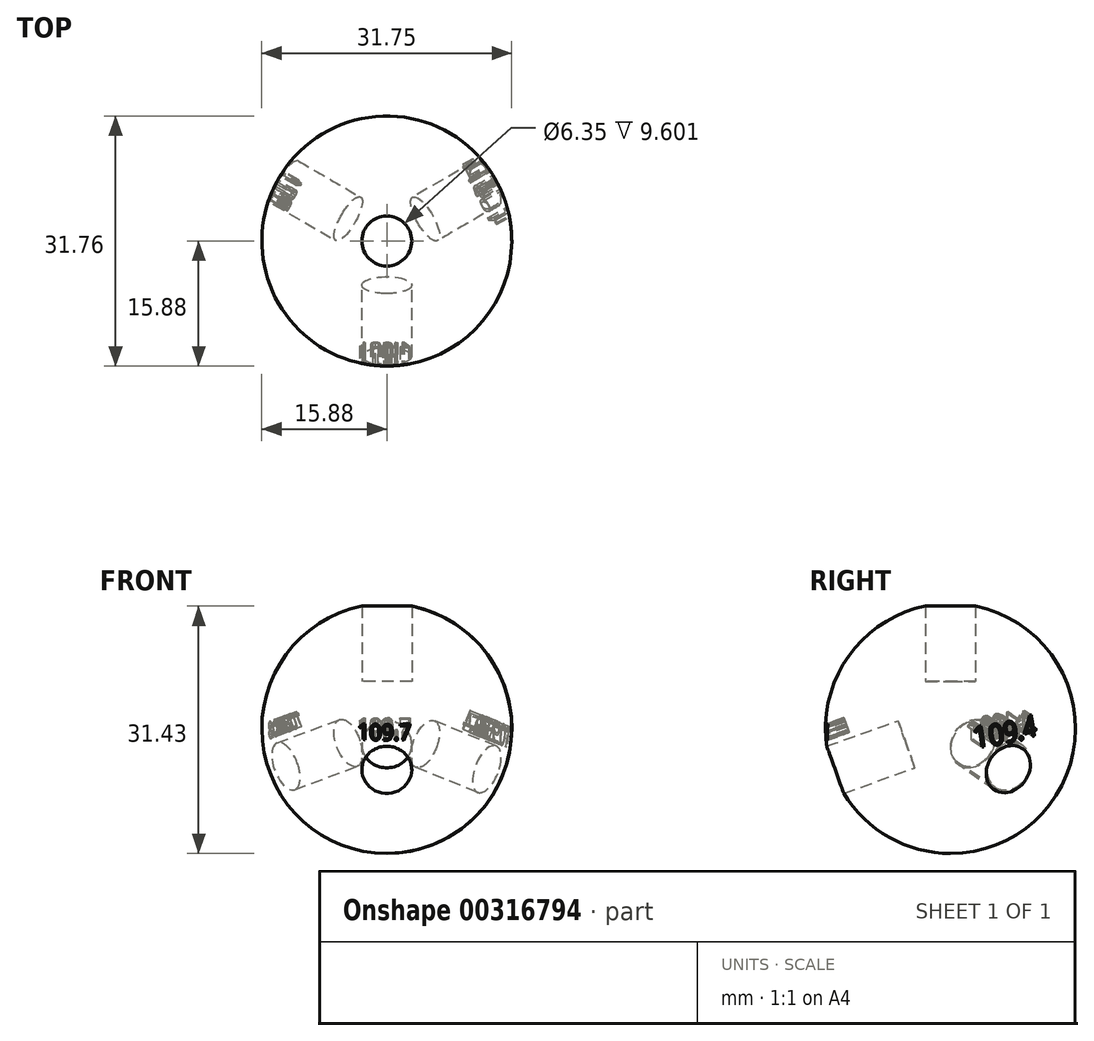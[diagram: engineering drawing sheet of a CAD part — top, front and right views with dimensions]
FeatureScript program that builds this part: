
annotation { "Feature Type Name" : "Feature", "Feature Type Description" : "" }
export const myFeature = defineFeature(function(context is Context, id is Id, definition is map)
    precondition{}
    {
        {
            var Q0;
            Q0=qCreatedBy(makeId("Front.planeOp"),FACE);
            var sketch = newSketch(context, id + "F0", { "sketchPlane" : qUnion([Q0])});
            skArc(sketch, "E0", {"start": v(0, 15.88) * mm, "mid": v(-15.88, 0) * mm, "end": v(0, -15.88) * mm});
            skLineSegment(sketch, "E1", {"start": v(0, 15.88) * mm, "end": v(0, -15.88) * mm});
            skSolve(sketch);
        }
        {
            var Q0;
            Q0 = qSketchRegion(id + "F0", true);
            var Q1;
            Q1=sQuery(id+"F0.wireOp",EDGE,"E1");
            revolve(context, id + "F1", {"entities" : qUnion([Q0]), "axis" : qUnion([Q1]), "revolveType" : RevolveType.FULL});
        }
        {
            var Q0;
            Q0=qCreatedBy(makeId("Top.planeOp"),FACE);
            cPlane(context, id + "F2", {"entities" : qUnion([Q0]), "cplaneType" : CPlaneType.OFFSET, "offset" : 5.95 * mm, "width" : 152.4 * mm, "height" : 152.4 * mm});
        }
        {
            var Q0;
            Q0=qCreatedBy(id+"F2.planeOp",FACE);
            var sketch = newSketch(context, id + "F3", { "sketchPlane" : qUnion([Q0])});
            skCircle(sketch, "E2", {"center": v(0, 0) * mm, "radius": 3.18 * mm});
            skSolve(sketch);
        }
        {
            var Q0;
            Q0 = qSketchRegion(id + "F3", true);
            extrude(context, id + "F4", {"entities" : qUnion([Q0]), "depth" : 25.4 * mm});
        }
        {
            var Q0;
            Q0=qCreatedBy(makeId("Front.planeOp"),FACE);
            var sketch = newSketch(context, id + "F5", { "sketchPlane" : qUnion([Q0])});
            skLineSegment(sketch, "E3", {"start": v(0, 0) * mm, "end": v(0, 41.69) * mm, "construction": true});
            skLineSegment(sketch, "E4", {"start": v(0, 41.69) * mm, "end": v(0, -35) * mm, "construction": true});
            skLineSegment(sketch, "E5", {"start": v(0, 0) * mm, "end": v(-50.95, 0) * mm, "construction": true});
            skLineSegment(sketch, "E6", {"start": v(-50.95, 0) * mm, "end": v(32.52, 0) * mm, "construction": true});
            skSolve(sketch);
        }
        {
            var Q0;
            Q0=qCreatedBy(makeId("Right.planeOp"),FACE);
            var sketch = newSketch(context, id + "F6", { "sketchPlane" : qUnion([Q0])});
            skLineSegment(sketch, "E7", {"start": v(0, 0) * mm, "end": v(52.26, 0) * mm, "construction": true});
            skLineSegment(sketch, "E8", {"start": v(52.26, 0) * mm, "end": v(-49.36, 0) * mm, "construction": true});
            skSolve(sketch);
        }
        {
            var Q0;
            Q0=makeQuery(id+"F4.opExtrude","SWEPT_BODY",BODY,{"disambiguationData":[OSD([sQuery(id+"F3.wireOp",EDGE,"E2")])]});
            var Q1;
            Q1=sQuery(id+"F5.wireOp",EDGE,"E6");
            transform(context, id + "F7", {"entities" : qUnion([Q0]), "transformType" : TransformType.ROTATION, "transformAxis" : qUnion([Q1]), "angle" : 109.7 * degree, "makeCopy" : true});
        }
        {
            var Q0;
            Q0=makeQuery(id+"F4.opExtrude","SWEPT_BODY",BODY,{"disambiguationData":[OSD([sQuery(id+"F3.wireOp",EDGE,"E2")])]});
            var Q1;
            Q1=sQuery(id+"F6.wireOp",EDGE,"E8");
            transform(context, id + "F8", {"entities" : qUnion([Q0]), "transformType" : TransformType.ROTATION, "transformAxis" : qUnion([Q1]), "angle" : 108 * degree, "makeCopy" : true});
        }
        {
            var Q0;
            Q0=makeQuery(id+"F8.opPattern","COPY",BODY,{"derivedFrom":makeQuery(id+"F4.opExtrude","SWEPT_BODY",BODY,{"disambiguationData":[OSD([sQuery(id+"F3.wireOp",EDGE,"E2")])]}),"instanceName":"1"});
            var Q1;
            Q1=sQuery(id+"F5.wireOp",EDGE,"E4");
            transform(context, id + "F9", {"entities" : qUnion([Q0]), "transformType" : TransformType.ROTATION, "transformAxis" : qUnion([Q1]), "angle" : 30 * degree, "makeCopy" : false});
        }
        {
            var Q0;
            Q0=makeQuery(id+"F7.opPattern","COPY",FACE,{"derivedFrom":makeQuery(id+"F4.opExtrude","CAP_FACE",FACE,{"disambiguationData":[OSD([sQuery(id+"F3.wireOp",EDGE,"E2")])],"isStart":false}),"instanceName":"1"});
            cPlane(context, id + "F10", {"entities" : qUnion([Q0]), "cplaneType" : CPlaneType.OFFSET, "offset" : 12.7 * mm, "oppositeDirection" : true, "width" : 152.4 * mm, "height" : 152.4 * mm});
        }
        {
            var Q0;
            Q0=qCreatedBy(id+"F10.planeOp",FACE);
            var sketch = newSketch(context, id + "F11", { "sketchPlane" : qUnion([Q0])});
            skText(sketch, "E9", { "text": "109.7", "fontName": "OpenSans-Regular.ttf"});
            const initialGuessF11  = {"E9": [-0.00373, 0.00391, 1, 0, 0.00193]};
            skSetInitialGuess(sketch, initialGuessF11);
            skSolve(sketch);
        }
        {
            var Q0;
            Q0 = qSketchRegion(id + "F11", true);
            extrude(context, id + "F12", {"entities" : qUnion([Q0]), "operationType" : NewBodyOperationType.REMOVE, "oppositeDirection" : true, "depth" : 6.35 * mm});
        }
        {
            var Q0;
            Q0=makeQuery(id+"F8.opPattern","COPY",FACE,{"derivedFrom":makeQuery(id+"F4.opExtrude","CAP_FACE",FACE,{"disambiguationData":[OSD([sQuery(id+"F3.wireOp",EDGE,"E2")])],"isStart":false}),"instanceName":"1"});
            cPlane(context, id + "F13", {"entities" : qUnion([Q0]), "cplaneType" : CPlaneType.OFFSET, "offset" : 12.7 * mm, "oppositeDirection" : true, "width" : 152.4 * mm, "height" : 152.4 * mm});
        }
        {
            var Q0;
            Q0=qCreatedBy(id+"F13.planeOp",FACE);
            var sketch = newSketch(context, id + "F14", { "sketchPlane" : qUnion([Q0])});
            skText(sketch, "E10", { "text": "108", "fontName": "OpenSans-Regular.ttf"});
            const initialGuessF14  = {"E10": [-0.0024, 0.00402, 1, 0, 0.00202]};
            skSetInitialGuess(sketch, initialGuessF14);
            skSolve(sketch);
        }
        {
            var Q0;
            Q0 = qSketchRegion(id + "F14", true);
            extrude(context, id + "F15", {"entities" : qUnion([Q0]), "operationType" : NewBodyOperationType.REMOVE, "oppositeDirection" : true, "depth" : 6.35 * mm});
        }
        {
            var Q0;
            Q0=makeQuery(id+"F4.opExtrude","SWEPT_BODY",BODY,{"disambiguationData":[OSD([sQuery(id+"F3.wireOp",EDGE,"E2")])]});
            var Q1;
            Q1=sQuery(id+"F6.wireOp",EDGE,"E7");
            transform(context, id + "F16", {"entities" : qUnion([Q0]), "transformType" : TransformType.ROTATION, "transformAxis" : qUnion([Q1]), "angle" : 109.4 * degree, "makeCopy" : true});
        }
        {
            var Q0;
            Q0=makeQuery(id+"F16.opPattern","COPY",BODY,{"derivedFrom":makeQuery(id+"F4.opExtrude","SWEPT_BODY",BODY,{"disambiguationData":[OSD([sQuery(id+"F3.wireOp",EDGE,"E2")])]}),"instanceName":"1"});
            var Q1;
            Q1=sQuery(id+"F5.wireOp",EDGE,"E4");
            transform(context, id + "F17", {"entities" : qUnion([Q0]), "transformType" : TransformType.ROTATION, "transformAxis" : qUnion([Q1]), "angle" : 30 * degree, "oppositeDirection" : true, "makeCopy" : false});
        }
        {
            var Q0;
            Q0=makeQuery(id+"F16.opPattern","COPY",FACE,{"derivedFrom":makeQuery(id+"F4.opExtrude","CAP_FACE",FACE,{"disambiguationData":[OSD([sQuery(id+"F3.wireOp",EDGE,"E2")])],"isStart":false}),"instanceName":"1"});
            cPlane(context, id + "F18", {"entities" : qUnion([Q0]), "cplaneType" : CPlaneType.OFFSET, "offset" : 12.7 * mm, "oppositeDirection" : true, "width" : 152.4 * mm, "height" : 152.4 * mm});
        }
        {
            var Q0;
            Q0=qCreatedBy(id+"F18.planeOp",FACE);
            var sketch = newSketch(context, id + "F19", { "sketchPlane" : qUnion([Q0])});
            skText(sketch, "E11", { "text": "109.4", "fontName": "OpenSans-Regular.ttf"});
            const initialGuessF19  = {"E11": [-0.0045, 0.00356, 1, 0, 0.00255]};
            skSetInitialGuess(sketch, initialGuessF19);
            skSolve(sketch);
        }
        {
            var Q0;
            Q0 = qSketchRegion(id + "F19", true);
            extrude(context, id + "F20", {"entities" : qUnion([Q0]), "operationType" : NewBodyOperationType.REMOVE, "oppositeDirection" : true, "depth" : 6.35 * mm});
        }
        {
            var Q0;
            Q0=makeQuery(id+"F7.opPattern","COPY",BODY,{"derivedFrom":makeQuery(id+"F4.opExtrude","SWEPT_BODY",BODY,{"disambiguationData":[OSD([sQuery(id+"F3.wireOp",EDGE,"E2")])]}),"instanceName":"1"});
            var Q1;
            Q1=makeQuery(id+"F8.opPattern","COPY",BODY,{"derivedFrom":makeQuery(id+"F4.opExtrude","SWEPT_BODY",BODY,{"disambiguationData":[OSD([sQuery(id+"F3.wireOp",EDGE,"E2")])]}),"instanceName":"1"});
            var Q2;
            Q2=makeQuery(id+"F16.opPattern","COPY",BODY,{"derivedFrom":makeQuery(id+"F4.opExtrude","SWEPT_BODY",BODY,{"disambiguationData":[OSD([sQuery(id+"F3.wireOp",EDGE,"E2")])]}),"instanceName":"1"});
            var Q3;
            Q3=makeQuery(id+"F4.opExtrude","SWEPT_BODY",BODY,{"disambiguationData":[OSD([sQuery(id+"F3.wireOp",EDGE,"E2")])]});
            var Q4;
            Q4=makeQuery(id+"F1.opRevolve","SWEPT_BODY",BODY,{"disambiguationData":[OSD([sQuery(id+"F0.wireOp",EDGE,"E0"),sQuery(id+"F0.wireOp",EDGE,"E1")])]});
            booleanBodies(context, id + "F21", {"operationType" : BooleanOperationType.SUBTRACTION, "tools" : qUnion([Q0, Q1, Q2, Q3]), "targets" : qUnion([Q4])});
        }
    });
